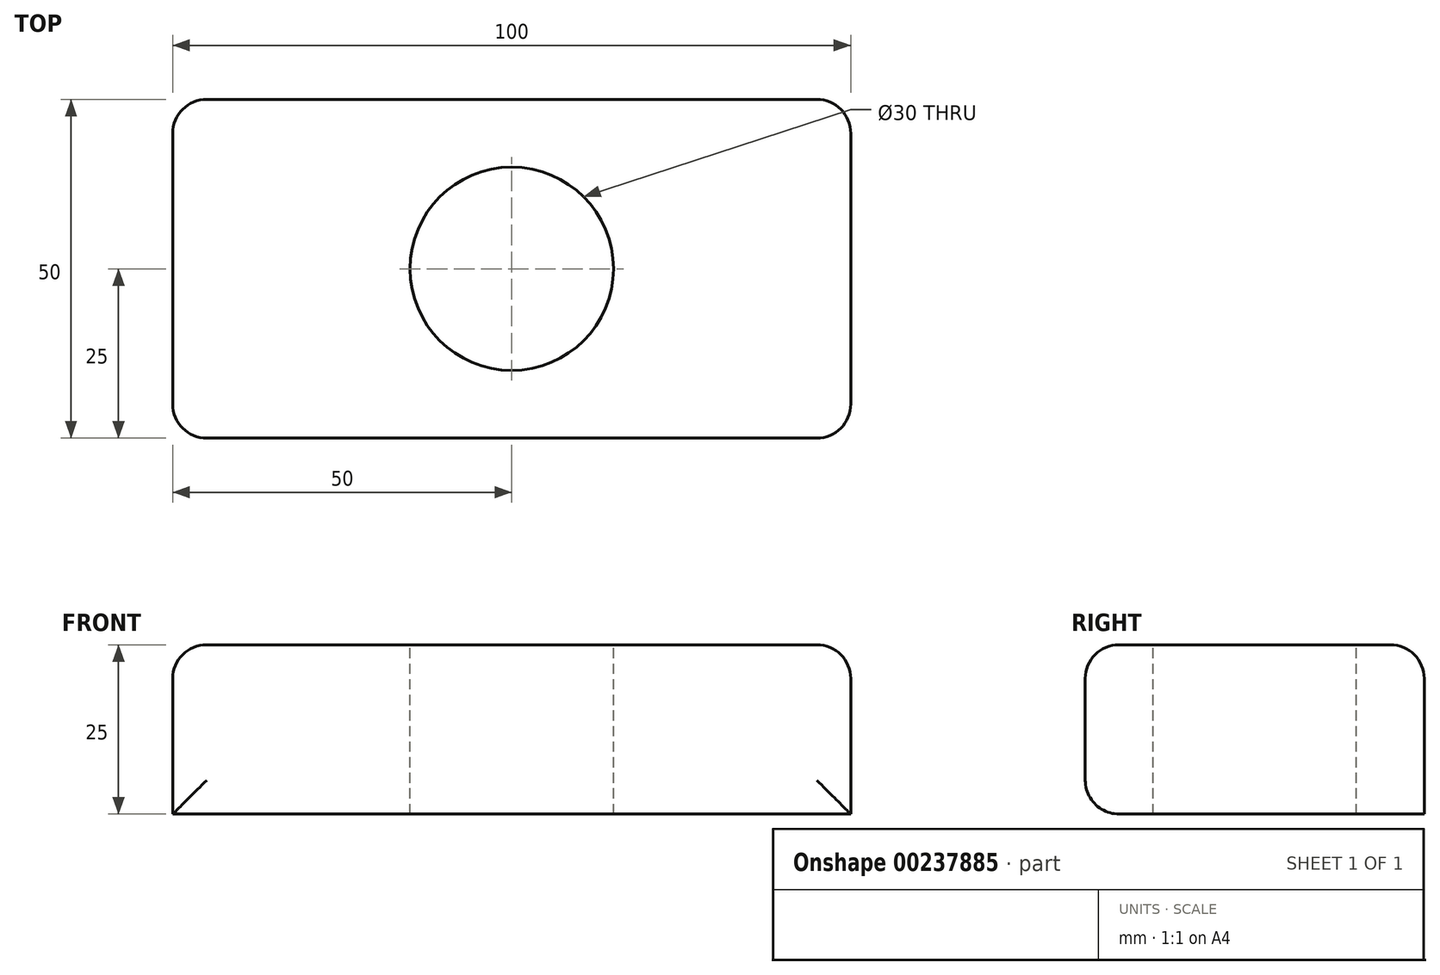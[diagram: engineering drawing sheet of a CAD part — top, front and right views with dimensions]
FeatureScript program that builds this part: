
annotation { "Feature Type Name" : "Feature", "Feature Type Description" : "" }
export const myFeature = defineFeature(function(context is Context, id is Id, definition is map)
    precondition{}
    {
        {
            var Q0;
            Q0=qCreatedBy(makeId("Top.planeOp"),FACE);
            var sketch = newSketch(context, id + "F0", { "sketchPlane" : qUnion([Q0])});
            skLineSegment(sketch, "E0.bottom", {"start": v(-50, -25) * mm, "end": v(50, -25) * mm});
            skLineSegment(sketch, "E0.top", {"start": v(-50, 25) * mm, "end": v(50, 25) * mm});
            skLineSegment(sketch, "E0.left", {"start": v(-50, -25) * mm, "end": v(-50, 25) * mm});
            skLineSegment(sketch, "E0.right", {"start": v(50, -25) * mm, "end": v(50, 25) * mm});
            skPoint(sketch, "E0.middle", {"position": v(0, 0) * mm});
            skSolve(sketch);
        }
        {
            var Q0;
            Q0 = qSketchRegion(id + "F0", true);
            extrude(context, id + "F1", {"entities" : qUnion([Q0]), "depth" : 25 * mm});
        }
        {
            var Q0;
            Q0=makeQuery(id+"F1.opExtrude","CAP_FACE",FACE,{"disambiguationData":[OSD([sQuery(id+"F0.wireOp",EDGE,"E0.bottom"),sQuery(id+"F0.wireOp",EDGE,"E0.top"),sQuery(id+"F0.wireOp",EDGE,"E0.left"),sQuery(id+"F0.wireOp",EDGE,"E0.right")])],"isStart":false});
            var sketch = newSketch(context, id + "F2", { "sketchPlane" : qUnion([Q0])});
            skCircle(sketch, "E1", {"center": v(0, 0) * mm, "radius": 15 * mm});
            skSolve(sketch);
        }
        {
            var Q0;
            Q0 = qSketchRegion(id + "F2", true);
            extrude(context, id + "F3", {"entities" : qUnion([Q0]), "operationType" : NewBodyOperationType.REMOVE, "endBound" : BoundingType.THROUGH_ALL, "oppositeDirection" : true, "depth" : 25 * mm});
        }
        {
            var Q0;
            Q0=makeQuery(id+"F1.opExtrude","CAP_EDGE",EDGE,{"disambiguationData":[OSD([sQuery(id+"F0.wireOp",EDGE,"E0.top")])],"isStart":false});
            var Q1;
            Q1=makeQuery(id+"F1.opExtrude","CAP_EDGE",EDGE,{"disambiguationData":[OSD([sQuery(id+"F0.wireOp",EDGE,"E0.left")])],"isStart":false});
            var Q2;
            Q2=makeQuery(id+"F1.opExtrude","SWEPT_FACE",FACE,{"disambiguationData":[OSD([sQuery(id+"F0.wireOp",EDGE,"E0.bottom")])]});
            var Q3;
            Q3=makeQuery(id+"F1.opExtrude","CAP_EDGE",EDGE,{"disambiguationData":[OSD([sQuery(id+"F0.wireOp",EDGE,"E0.right")])],"isStart":false});
            fillet(context, id + "F4", {"entities" : qUnion([Q0, Q1, Q2, Q3]), "radius" : 5 * mm, "tangentPropagation" : true, "allowEdgeOverflow" : false});
        }
        {
            var Q0;
            Q0=makeQuery(id+"F4.opFillet","BLEND_EDGE",EDGE,{"blendedFrom":[makeQuery(id+"F1.opExtrude","CAP_EDGE",EDGE,{"disambiguationData":[OSD([sQuery(id+"F0.wireOp",EDGE,"E0.top")])],"isStart":false}),makeQuery(id+"F1.opExtrude","CAP_EDGE",EDGE,{"disambiguationData":[OSD([sQuery(id+"F0.wireOp",EDGE,"E0.left")])],"isStart":false})],"blendedInto":[]});
            fillet(context, id + "F5", {"entities" : qUnion([Q0]), "radius" : 5 * mm, "tangentPropagation" : true, "allowEdgeOverflow" : false});
        }
        {
            var Q0;
            Q0=makeQuery(id+"F4.opFillet","BLEND_EDGE",EDGE,{"blendedFrom":[makeQuery(id+"F1.opExtrude","CAP_EDGE",EDGE,{"disambiguationData":[OSD([sQuery(id+"F0.wireOp",EDGE,"E0.top")])],"isStart":false}),makeQuery(id+"F1.opExtrude","CAP_EDGE",EDGE,{"disambiguationData":[OSD([sQuery(id+"F0.wireOp",EDGE,"E0.right")])],"isStart":false})],"blendedInto":[]});
            fillet(context, id + "F6", {"entities" : qUnion([Q0]), "radius" : 5 * mm, "tangentPropagation" : true, "allowEdgeOverflow" : false});
        }
    });
